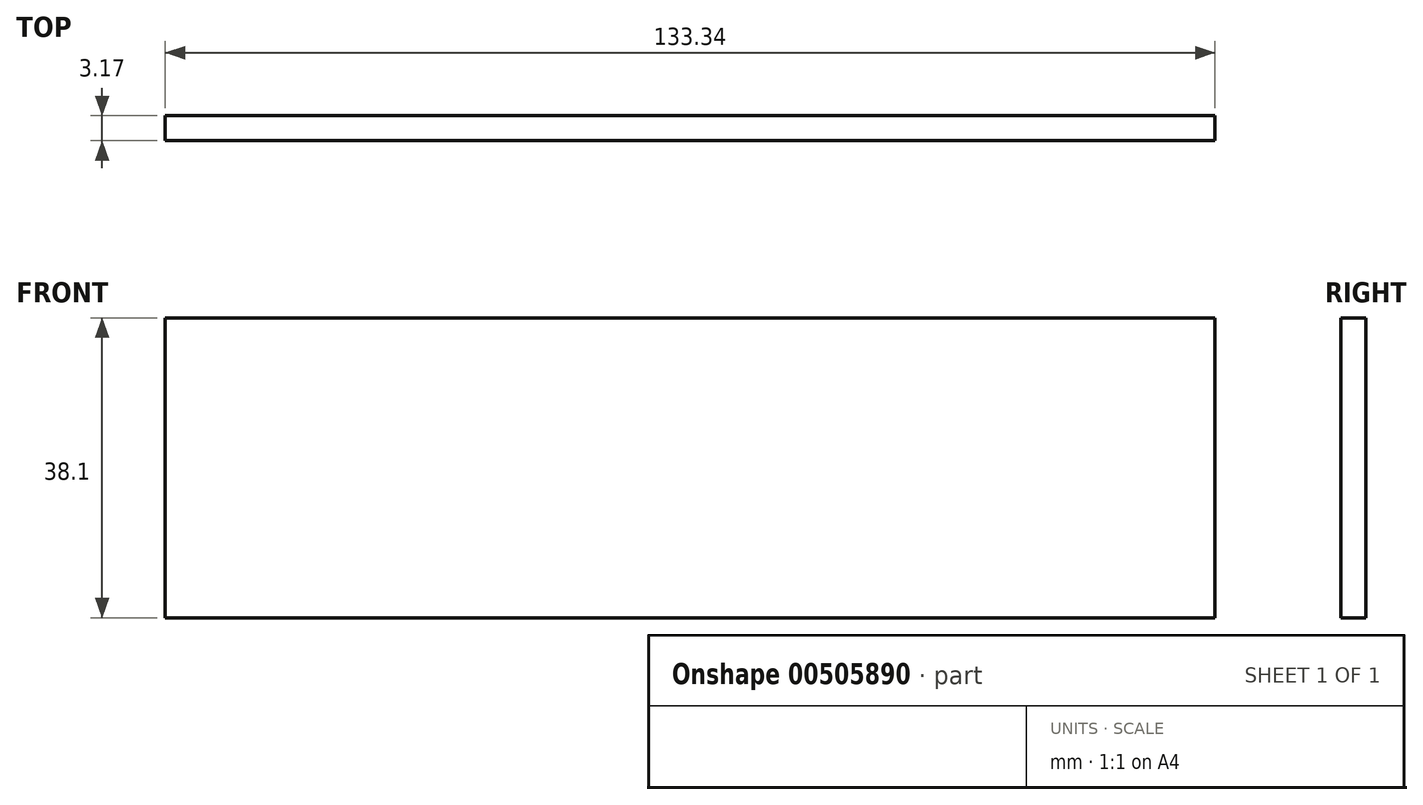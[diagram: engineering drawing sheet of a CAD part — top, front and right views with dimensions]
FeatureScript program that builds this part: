
annotation { "Feature Type Name" : "Feature", "Feature Type Description" : "" }
export const myFeature = defineFeature(function(context is Context, id is Id, definition is map)
    precondition{}
    {
        {
            var Q0;
            Q0=qCreatedBy(makeId("Front.planeOp"),FACE);
            var sketch = newSketch(context, id + "F0", { "sketchPlane" : qUnion([Q0])});
            skLineSegment(sketch, "E0.bottom", {"start": v(-28.58, 19.05) * mm, "end": v(28.58, 19.05) * mm});
            skLineSegment(sketch, "E0.top", {"start": v(-28.58, -19.05) * mm, "end": v(28.58, -19.05) * mm});
            skLineSegment(sketch, "E1.bottom", {"start": v(-28.58, 19.05) * mm, "end": v(-66.68, 19.05) * mm});
            skLineSegment(sketch, "E1.top", {"start": v(-28.58, -19.05) * mm, "end": v(-66.68, -19.05) * mm});
            skLineSegment(sketch, "E1.right", {"start": v(-66.68, 19.05) * mm, "end": v(-66.68, -19.05) * mm});
            skLineSegment(sketch, "E2.bottom", {"start": v(28.58, -19.05) * mm, "end": v(66.67, -19.05) * mm});
            skLineSegment(sketch, "E2.top", {"start": v(28.58, 19.05) * mm, "end": v(66.68, 19.05) * mm});
            skLineSegment(sketch, "E2.right", {"start": v(66.67, -19.05) * mm, "end": v(66.67, 19.05) * mm});
            skSolve(sketch);
        }
        {
            var Q0;
            Q0=makeQuery(id+"F0.imprint","IMPRINT",FACE,{"disambiguationData":[TD([[makeQuery(id+"F0.imprint","IMPRINT",EDGE,{"derivedFrom":sQuery(id+"F0.wireOp",EDGE,"E0.bottom")}),-1.0]])]});
            extrude(context, id + "F1", {"entities" : qUnion([Q0]), "depth" : 3.17 * mm});
        }
    });
